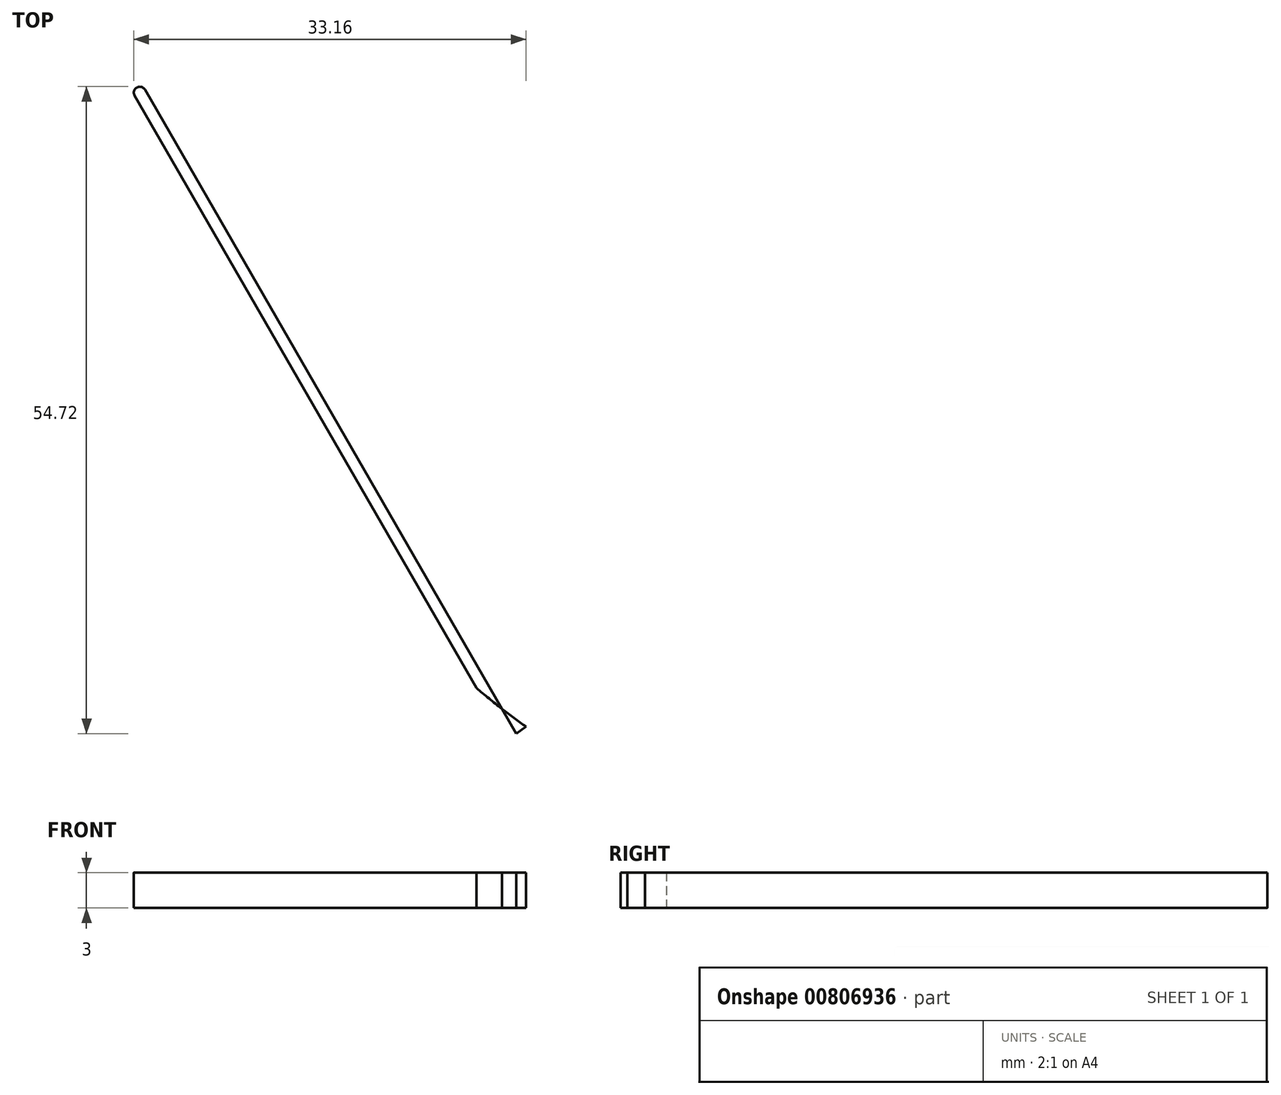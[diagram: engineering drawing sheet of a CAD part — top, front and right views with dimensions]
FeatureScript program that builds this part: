
annotation { "Feature Type Name" : "Feature", "Feature Type Description" : "" }
export const myFeature = defineFeature(function(context is Context, id is Id, definition is map)
    precondition{}
    {
        {
            var Q0;
            Q0=qCreatedBy(makeId("Top.planeOp"),FACE);
            var sketch = newSketch(context, id + "F0", { "sketchPlane" : qUnion([Q0])});
            skArc(sketch, "E0", {"start": v(-1.05, -2.9) * mm, "mid": v(3.06, -0.4) * mm, "end": v(-0.27, 3.07) * mm});
            skPoint(sketch, "E1", {"position": v(-24.96, 5.96) * mm});
            skLineSegment(sketch, "E2.0.startCap", {"start": v(-3.08, 2.46) * mm, "end": v(-3.08, 2.46) * mm});
            skFitSpline(sketch, "E2.0.right", {"points": [v(-2.67, 2.5) * mm, v(-5.5, 2.17) * mm, v(-11.3, 2.55) * mm, v(-18.7, 5.62) * mm, v(-24.55, 9.62) * mm, v(-28.86, 13.39) * mm, v(-33.04, 17.92) * mm, v(-38.47, 24.92) * mm, v(-45, 35.3) * mm, v(-52.5, 49.78) * mm, v(-59.8, 65.75) * mm, v(-64.62, 77.03) * mm, v(-67.04, 82.73) * mm]});
            skFitSpline(sketch, "E3", {"points": [v(-3.08, 2.46) * mm, v(-0.27, 3.07) * mm], "startDerivative": vector(4, 0.43) * mm, "endDerivative": vector(4.02, 0.35) * mm});
            skFitSpline(sketch, "E4", {"points": [v(-7.23, -0.55) * mm, v(-1.05, -2.9) * mm], "startDerivative": vector(9.7, -1.02) * mm, "endDerivative": vector(6.76, -2.44) * mm});
            skLineSegment(sketch, "E5", {"start": v(-24.63, 6.2) * mm, "end": v(-23.88, 6.73) * mm});
            skFitSpline(sketch, "E6.trimOffspring", {"points": [v(-2.2, -0.45) * mm, v(-5.41, -0.82) * mm, v(-11.94, -0.38) * mm, v(-20.02, 3) * mm, v(-26.29, 7.28) * mm, v(-30.85, 11.27) * mm, v(-35.23, 16.02) * mm, v(-40.85, 23.26) * mm, v(-47.5, 33.85) * mm, v(-55.1, 48.5) * mm, v(-62.45, 64.57) * mm, v(-67.28, 75.88) * mm, v(-69.7, 81.59) * mm]});
            skPoint(sketch, "E7.startDerivative.orphan", {"position": v(-12.14, 0) * mm});
            skArc(sketch, "E8.0.endCap", {"start": v(-55.35, 61.28) * mm, "mid": v(-55.16, 61.96) * mm, "end": v(-54.48, 61.77) * mm});
            skLineSegment(sketch, "E8.0.left", {"start": v(-23.88, 6.73) * mm, "end": v(-55.35, 61.28) * mm});
            skLineSegment(sketch, "E8.0.right", {"start": v(-23.06, 7.31) * mm, "end": v(-54.48, 61.77) * mm});
            skLineSegment(sketch, "E9.trimOffspring", {"start": v(-23.06, 7.31) * mm, "end": v(-22.12, 7.99) * mm});
            skSolve(sketch);
        }
        {
            var Q0;
            Q0=qSketchRegion(id+"F0",true);
            extrude(context, id + "F1", {"entities" : qUnion([Q0]), "endBound" : BoundingType.SYMMETRIC, "depth" : 3 * mm, "offsetDistance" : 25 * mm});
        }
        {
            var Q0;
            Q0=makeQuery(id+"F1.opExtrude","CAP_FACE",FACE,{"disambiguationData":[OSD([sQuery(id+"F0.wireOp",EDGE,"E0"),sQuery(id+"F0.wireOp",EDGE,"E2.0.right"),sQuery(id+"F0.wireOp",EDGE,"E3"),sQuery(id+"F0.wireOp",EDGE,"E4"),sQuery(id+"F0.wireOp",EDGE,"E5"),sQuery(id+"F0.wireOp",EDGE,"E6.trimOffspring"),sQuery(id+"F0.wireOp",EDGE,"E8.0.endCap"),sQuery(id+"F0.wireOp",EDGE,"E8.0.left"),sQuery(id+"F0.wireOp",EDGE,"E8.0.right"),sQuery(id+"F0.wireOp",EDGE,"E9.trimOffspring")])],"isStart":true});
            var sketch = newSketch(context, id + "F2", { "sketchPlane" : qUnion([Q0])});
            skCircle(sketch, "E10", {"center": v(0, 0) * mm, "radius": 1.5 * mm});
            skSolve(sketch);
        }
        {
            var Q0;
            Q0=qSketchRegion(id+"F2",true);
            extrude(context, id + "F3", {"entities" : qUnion([Q0]), "operationType" : NewBodyOperationType.REMOVE, "oppositeDirection" : true, "depth" : 25 * mm, "offsetDistance" : 25 * mm});
        }
    });
